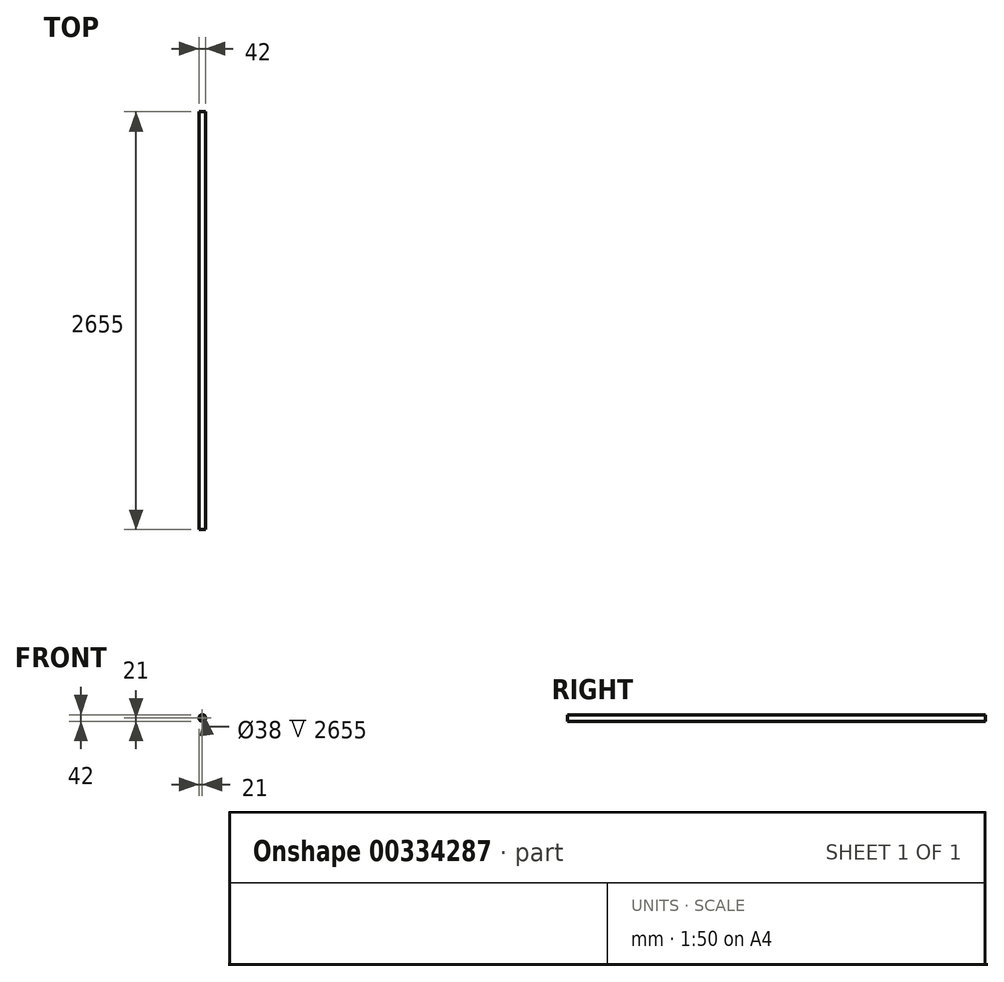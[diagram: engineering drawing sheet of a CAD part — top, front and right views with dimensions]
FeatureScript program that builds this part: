
annotation { "Feature Type Name" : "Feature", "Feature Type Description" : "" }
export const myFeature = defineFeature(function(context is Context, id is Id, definition is map)
    precondition{}
    {
        {
            assignVariable(context, id + "F0", {"name" : "L", "anyValue" : 2655});
        }
        {
            var Q0;
            Q0=qCreatedBy(makeId("Front.planeOp"),FACE);
            var sketch = newSketch(context, id + "F1", { "sketchPlane" : qUnion([Q0])});
            skCircle(sketch, "E0", {"center": v(0, 0) * mm, "radius": 21 * mm});
            skCircle(sketch, "E1", {"center": v(0, 0) * mm, "radius": 19 * mm});
            skSolve(sketch);
        }
        {
            var Q0;
            Q0=makeQuery(id+"F1.imprint","IMPRINT",FACE,{"disambiguationData":[TD([[makeQuery(id+"F1.imprint","IMPRINT",EDGE,{"derivedFrom":sQuery(id+"F1.wireOp",EDGE,"E0")}),1.0]])]});
            extrude(context, id + "F2", {"entities" : qUnion([Q0]), "depth" : (getVariable(context, 'L')) * mm});
        }
    });
